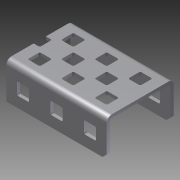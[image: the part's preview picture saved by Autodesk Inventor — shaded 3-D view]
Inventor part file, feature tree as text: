
AUTODESK INVENTOR PART (.ipt)
format: ipt  version: 2014 SP1 (Build 180222100, 222)  size: 350,208 bytes
history: native  units: in
note: dims shown in document units (in); Inventor stores cm internally (conversion verified against a paired STEP export)
features: other x1, imported_body x1, extrude x1, sketch x1
ambient origin geometry x8: Origin, YZ Plane, XZ Plane, XY Plane, X Axis, Y Axis, Z Axis, Center Point
bodies: Body1 (feature_tree)
feature tree (4):
  parser-record x1  (decoder bookkeeping rows leaked as tree rows — omitted from the tree; the rows remain in map.json)
  imported_body  "Base1"
  extrude  "Extrusion1"  Depth=1.0in TaperAngle=0.0deg
  sketch  "Sketch1"  dims[d0=1.0in d1=1.0in d2=0.0in]
